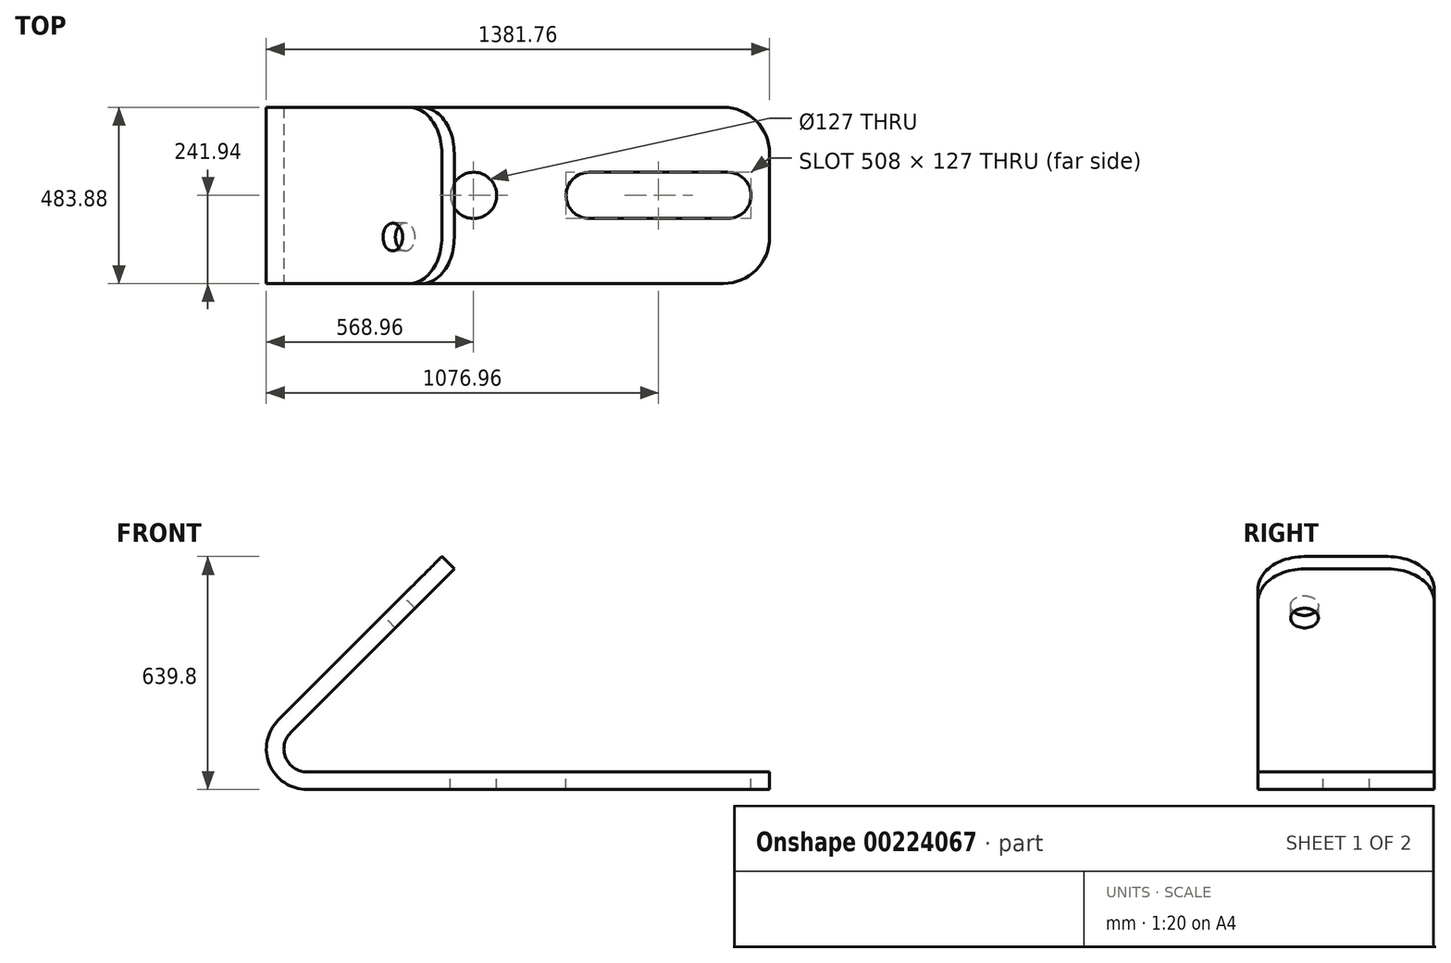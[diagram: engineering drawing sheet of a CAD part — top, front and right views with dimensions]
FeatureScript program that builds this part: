
annotation { "Feature Type Name" : "Feature", "Feature Type Description" : "" }
export const myFeature = defineFeature(function(context is Context, id is Id, definition is map)
    precondition{}
    {
        {
            var Q0;
            Q0=qCreatedBy(makeId("Front.planeOp"),FACE);
            var sketch = newSketch(context, id + "F0", { "sketchPlane" : qUnion([Q0])});
            skLineSegment(sketch, "E0", {"start": v(0, 0) * mm, "end": v(-1270, 0) * mm});
            skLineSegment(sketch, "E1", {"start": v(-1270, 0) * mm, "end": v(-1381.76, 0) * mm, "construction": true});
            skLineSegment(sketch, "E2", {"start": v(-1381.76, 0) * mm, "end": v(-1381.76, 111.76) * mm, "construction": true});
            skLineSegment(sketch, "E3", {"start": v(-1349.03, 190.79) * mm, "end": v(-900.01, 639.8) * mm});
            skLineSegment(sketch, "E4", {"start": v(-900.01, 639.8) * mm, "end": v(-865.89, 605.67) * mm});
            skArc(sketch, "E5", {"start": v(-1349.03, 190.79) * mm, "mid": v(-1373.25, 69) * mm, "end": v(-1270, 0) * mm});
            skLineSegment(sketch, "E6", {"start": v(-865.89, 605.67) * mm, "end": v(-1314.9, 156.66) * mm});
            skLineSegment(sketch, "E7", {"start": v(0, 0) * mm, "end": v(0, 48.26) * mm});
            skLineSegment(sketch, "E8", {"start": v(0, 48.26) * mm, "end": v(-1270, 48.26) * mm});
            skArc(sketch, "E9", {"start": v(-1314.9, 156.66) * mm, "mid": v(-1328.67, 87.46) * mm, "end": v(-1270, 48.26) * mm});
            skSolve(sketch);
        }
        {
            var Q0;
            Q0=makeQuery(id+"F0.imprint","IMPRINT",FACE,{"disambiguationData":[TD([[makeQuery(id+"F0.imprint","IMPRINT",EDGE,{"derivedFrom":sQuery(id+"F0.wireOp",EDGE,"E0")}),-1.0]])]});
            extrude(context, id + "F1", {"entities" : qUnion([Q0]), "endBound" : BoundingType.SYMMETRIC, "oppositeDirection" : true, "depth" : 483.87 * mm});
        }
        {
            var Q0;
            Q0=makeQuery(id+"F1.opExtrude","SWEPT_FACE",FACE,{"disambiguationData":[OSD([sQuery(id+"F0.wireOp",EDGE,"E8")])]});
            var sketch = newSketch(context, id + "F2", { "sketchPlane" : qUnion([Q0])});
            skLineSegment(sketch, "E10", {"start": v(0, 0) * mm, "end": v(-812.8, 0) * mm, "construction": true});
            skPoint(sketch, "E10.endSnap0", {"position": v(0, 0) * mm});
            skCircle(sketch, "E11", {"center": v(-812.8, 0) * mm, "radius": 63.5 * mm});
            skLineSegment(sketch, "E12", {"start": v(0, 0) * mm, "end": v(-114.3, 0) * mm, "construction": true});
            skLineSegment(sketch, "E13", {"start": v(-114.3, 0) * mm, "end": v(-495.3, 0) * mm, "construction": true});
            skCircle(sketch, "E14", {"center": v(-495.3, 0) * mm, "radius": 63.5 * mm});
            skCircle(sketch, "E15", {"center": v(-114.3, 0) * mm, "radius": 63.5 * mm});
            skLineSegment(sketch, "E16", {"start": v(-495.3, 63.5) * mm, "end": v(-114.3, 63.5) * mm});
            skLineSegment(sketch, "E17", {"start": v(-114.3, -63.5) * mm, "end": v(-495.3, -63.5) * mm});
            skSolve(sketch);
        }
        {
            var Q0;
            Q0=makeQuery(id+"F2.imprint","IMPRINT",FACE,{"disambiguationData":[TD([[makeQuery(id+"F2.imprint","IMPRINT",EDGE,{"derivedFrom":sQuery(id+"F2.wireOp",EDGE,"E11")}),1.0]])]});
            var Q1;
            {var subQ0=sQuery(id+"F2.wireOp",EDGE,"E14");var subQ1=makeQuery(id+"F2.imprint","INTERSECT",VERTEX,{"derivedFrom":[subQ0,sQuery(id+"F2.wireOp",EDGE,"E16")]});Q1=makeQuery(id+"F2.imprint","IMPRINT",FACE,{"disambiguationData":[TD([[makeQuery(id+"F2.imprint","IMPRINT",EDGE,{"disambiguationData":[TD([[subQ1,-1.0]])],"derivedFrom":subQ0}),1.0]])]});}
            var Q2;
            {var subQ0=sQuery(id+"F2.wireOp",EDGE,"E16");Q2=makeQuery(id+"F2.imprint","IMPRINT",FACE,{"disambiguationData":[TD([[makeQuery(id+"F2.imprint","IMPRINT",EDGE,{"derivedFrom":subQ0}),-1.0]])]});}
            var Q3;
            {var subQ0=sQuery(id+"F2.wireOp",EDGE,"E15");var subQ1=makeQuery(id+"F2.imprint","INTERSECT",VERTEX,{"derivedFrom":[subQ0,sQuery(id+"F2.wireOp",EDGE,"E16")]});Q3=makeQuery(id+"F2.imprint","IMPRINT",FACE,{"disambiguationData":[TD([[makeQuery(id+"F2.imprint","IMPRINT",EDGE,{"disambiguationData":[TD([[subQ1,-1.0]])],"derivedFrom":subQ0}),1.0]])]});}
            extrude(context, id + "F3", {"entities" : qUnion([Q0, Q1, Q2, Q3]), "operationType" : NewBodyOperationType.REMOVE, "endBound" : BoundingType.THROUGH_ALL, "oppositeDirection" : true, "depth" : 25.4 * mm});
        }
        {
            var Q0;
            Q0=makeQuery(id+"F1.opExtrude","SWEPT_FACE",FACE,{"disambiguationData":[OSD([sQuery(id+"F0.wireOp",EDGE,"E3")])]});
            var sketch = newSketch(context, id + "F4", { "sketchPlane" : qUnion([Q0])});
            skLineSegment(sketch, "E18", {"start": v(0, -184) * mm, "end": v(0, -374.5) * mm, "construction": true});
            skPoint(sketch, "E18.endSnap0", {"position": v(0, -184) * mm});
            skLineSegment(sketch, "E19", {"start": v(0, -374.5) * mm, "end": v(114.3, -374.5) * mm, "construction": true});
            skCircle(sketch, "E20", {"center": v(114.3, -374.5) * mm, "radius": 38.1 * mm});
            skSolve(sketch);
        }
        {
            var Q0;
            Q0 = qSketchRegion(id + "F4", true);
            extrude(context, id + "F5", {"entities" : qUnion([Q0]), "operationType" : NewBodyOperationType.REMOVE, "endBound" : BoundingType.UP_TO_NEXT, "oppositeDirection" : true, "depth" : 25.4 * mm});
        }
        {
            var Q0;
            Q0=makeQuery(id+"F1.opExtrude","CAP_EDGE",EDGE,{"disambiguationData":[OSD([sQuery(id+"F0.wireOp",EDGE,"E4")])],"isStart":false});
            var Q1;
            Q1=makeQuery(id+"F1.opExtrude","CAP_EDGE",EDGE,{"disambiguationData":[OSD([sQuery(id+"F0.wireOp",EDGE,"E4")])],"isStart":true});
            fillet(context, id + "F6", {"entities" : qUnion([Q0, Q1]), "radius" : 127 * mm, "tangentPropagation" : true, "allowEdgeOverflow" : false});
        }
        {
            var Q0;
            Q0=makeQuery(id+"F1.opExtrude","CAP_EDGE",EDGE,{"disambiguationData":[OSD([sQuery(id+"F0.wireOp",EDGE,"E7")])],"isStart":false});
            var Q1;
            Q1=makeQuery(id+"F1.opExtrude","CAP_EDGE",EDGE,{"disambiguationData":[OSD([sQuery(id+"F0.wireOp",EDGE,"E7")])],"isStart":true});
            fillet(context, id + "F7", {"entities" : qUnion([Q0, Q1]), "radius" : 127 * mm, "tangentPropagation" : true, "allowEdgeOverflow" : false});
        }
    });
